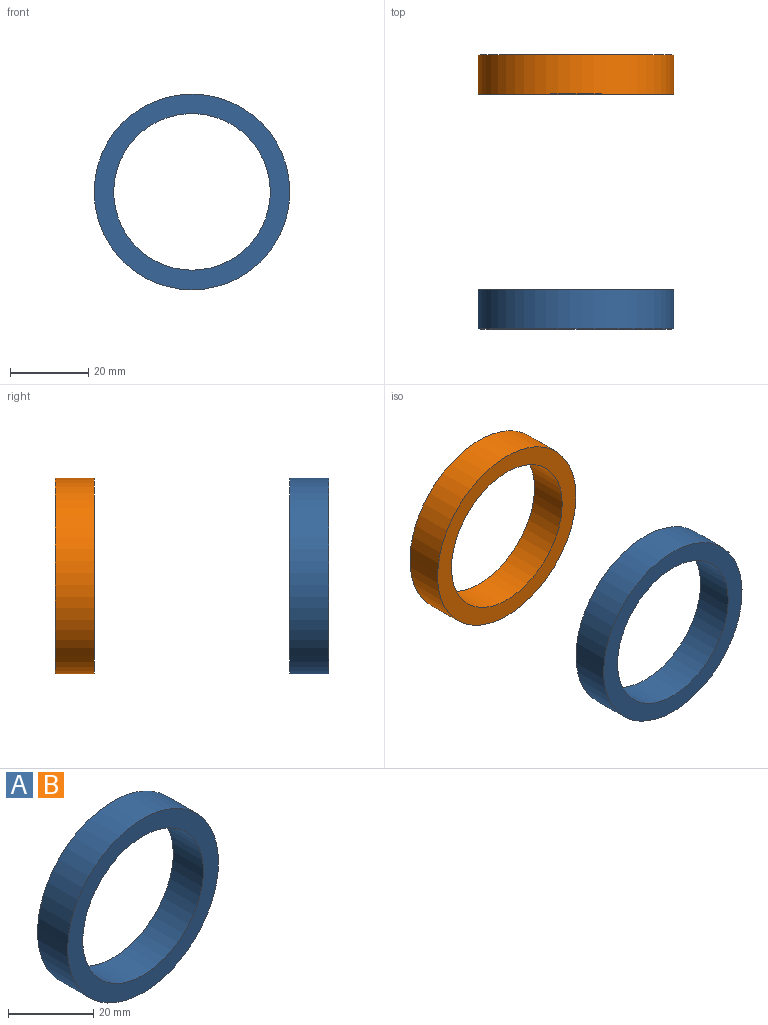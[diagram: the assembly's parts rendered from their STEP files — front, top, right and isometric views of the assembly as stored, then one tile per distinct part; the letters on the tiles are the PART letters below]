
ASSEMBLY  parts=2 mates=1
PART A: 4 faces, bbox 50x10x50 mm
  f0: cylinder r=20mm len=40mm, axis (0,1,0), area 1256.6mm2, adj f2,f3
  f1: cylinder r=25mm len=50mm, axis (0,1,0), area 1570.8mm2, adj f2,f3
  f2: plane 50x50mm, normal (0,-1,0), area 706.9mm2, adj f0,f1
  f3: plane 50x50mm, normal (0,1,0), area 706.9mm2, adj f0,f1
PART B: same geometry as A
PLACE A t=(0,-60,0)mm
PLACE B at identity fixed
MATE slider B.f1 <-> A.f1  axis (0,1,0) through (0,-10,0)mm
